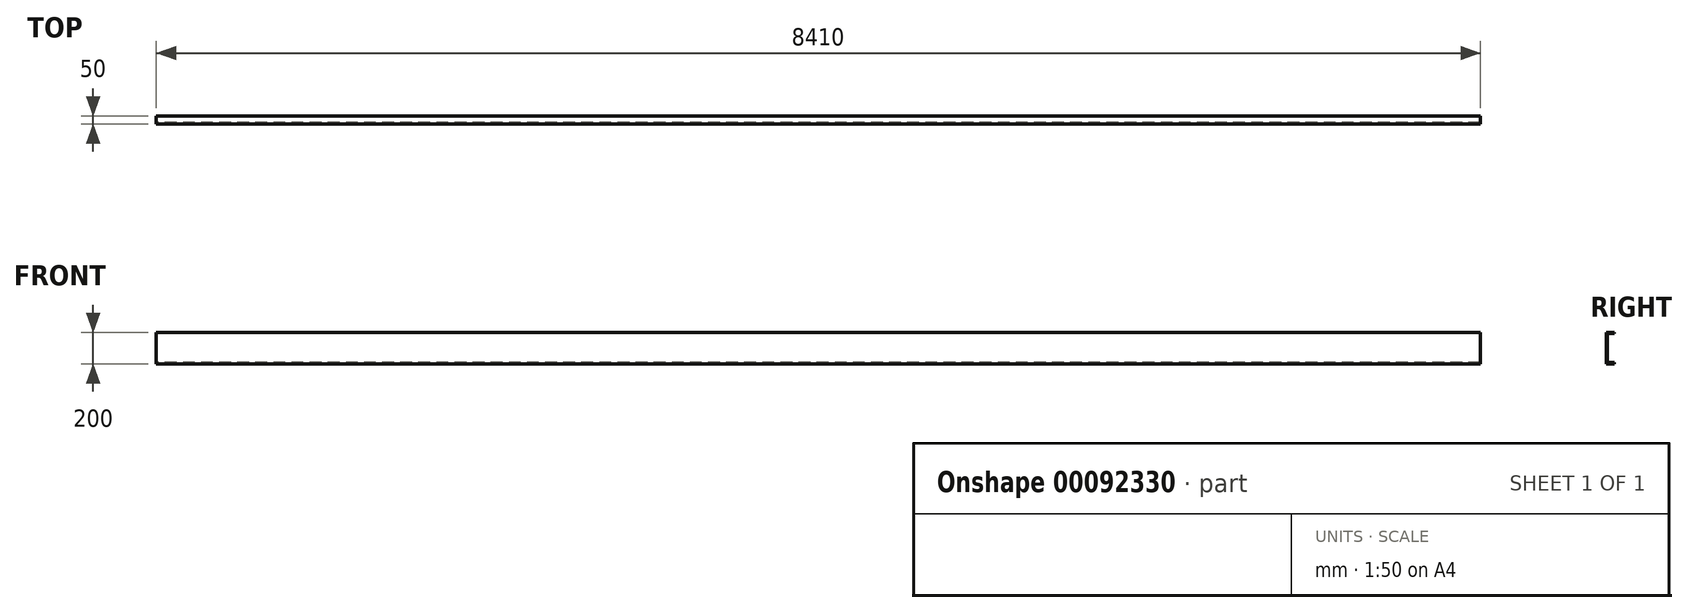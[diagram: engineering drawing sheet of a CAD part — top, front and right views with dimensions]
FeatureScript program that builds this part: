
annotation { "Feature Type Name" : "Feature", "Feature Type Description" : "" }
export const myFeature = defineFeature(function(context is Context, id is Id, definition is map)
    precondition{}
    {
        {
            var Q0;
            Q0=qCreatedBy(makeId("Right.planeOp"),FACE);
            var sketch = newSketch(context, id + "F0", { "sketchPlane" : qUnion([Q0])});
            skLineSegment(sketch, "E0", {"start": v(0, 0) * mm, "end": v(-50, 0) * mm});
            skLineSegment(sketch, "E1", {"start": v(-50, 0) * mm, "end": v(-50, 200) * mm});
            skLineSegment(sketch, "E2", {"start": v(-50, 200) * mm, "end": v(0, 200) * mm});
            skLineSegment(sketch, "E3", {"start": v(0, 200) * mm, "end": v(0, 192) * mm});
            skLineSegment(sketch, "E4", {"start": v(0, 192) * mm, "end": v(-42, 192) * mm});
            skLineSegment(sketch, "E5", {"start": v(-42, 192) * mm, "end": v(-42, 8) * mm});
            skLineSegment(sketch, "E6", {"start": v(-42, 8) * mm, "end": v(0, 8) * mm});
            skLineSegment(sketch, "E7", {"start": v(0, 8) * mm, "end": v(0, 0) * mm});
            skSolve(sketch);
        }
        {
            var Q0;
            Q0=qSketchRegion(id+"F0",true);
            extrude(context, id + "F1", {"entities" : qUnion([Q0]), "depth" : 8410 * mm});
        }
    });
